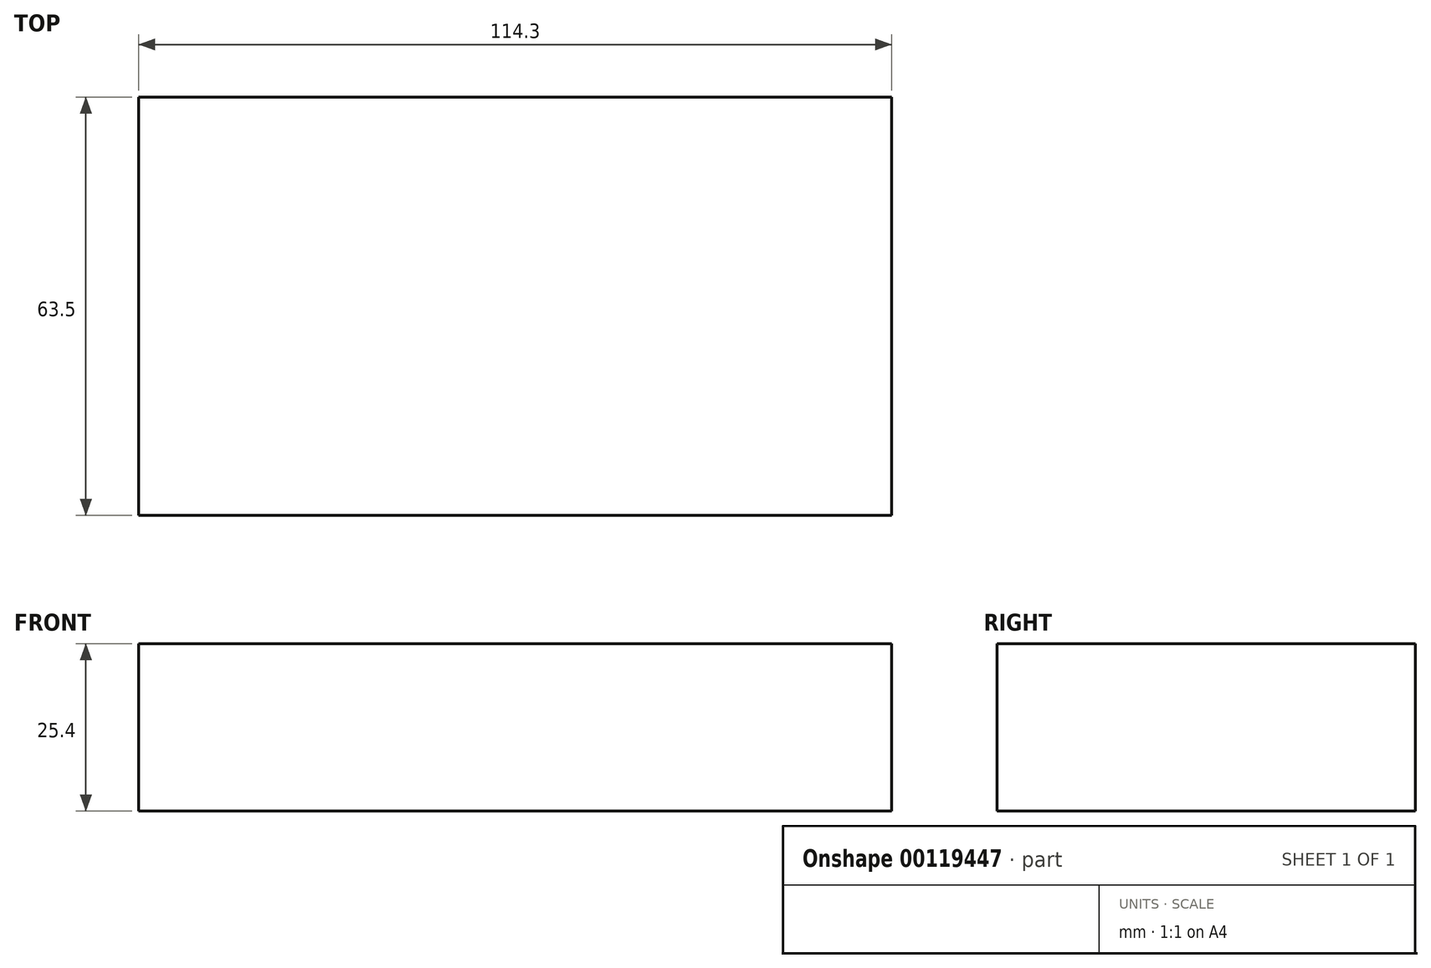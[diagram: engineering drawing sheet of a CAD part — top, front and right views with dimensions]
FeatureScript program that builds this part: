
annotation { "Feature Type Name" : "Feature", "Feature Type Description" : "" }
export const myFeature = defineFeature(function(context is Context, id is Id, definition is map)
    precondition{}
    {
        {
            var Q0;
            Q0=qCreatedBy(makeId("Top.planeOp"),FACE);
            var sketch = newSketch(context, id + "F0", { "sketchPlane" : qUnion([Q0])});
            skLineSegment(sketch, "E0.bottom", {"start": v(-114.3, 31.75) * mm, "end": v(0, 31.75) * mm});
            skLineSegment(sketch, "E0.top", {"start": v(-114.3, -31.75) * mm, "end": v(0, -31.75) * mm});
            skLineSegment(sketch, "E0.left", {"start": v(-114.3, 31.75) * mm, "end": v(-114.3, -31.75) * mm});
            skLineSegment(sketch, "E0.right", {"start": v(0, 31.75) * mm, "end": v(0, -31.75) * mm});
            skSolve(sketch);
        }
        {
            var Q0;
            Q0 = qSketchRegion(id + "F0", true);
            extrude(context, id + "F1", {"entities" : qUnion([Q0]), "depth" : 25.4 * mm});
        }
    });
